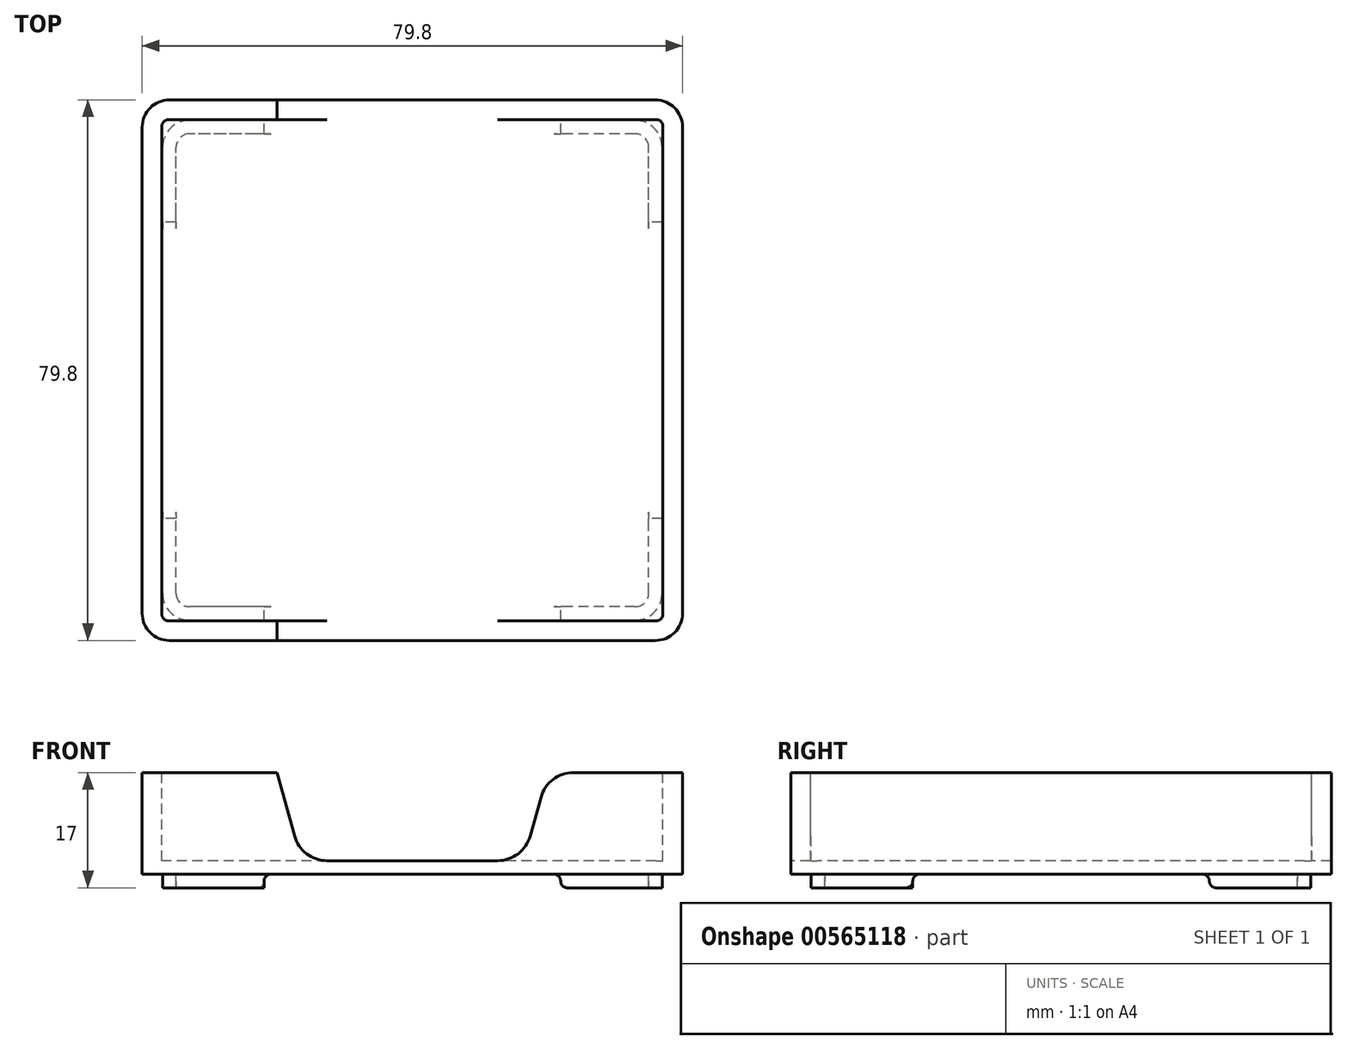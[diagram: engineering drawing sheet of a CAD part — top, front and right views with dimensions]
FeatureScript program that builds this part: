
annotation { "Feature Type Name" : "Feature", "Feature Type Description" : "" }
export const myFeature = defineFeature(function(context is Context, id is Id, definition is map)
    precondition{}
    {
        {
            var Q0;
            Q0=qCreatedBy(makeId("Top.planeOp"),FACE);
            var sketch = newSketch(context, id + "F0", { "sketchPlane" : qUnion([Q0])});
            skLineSegment(sketch, "E0.bottom", {"start": v(39.9, 39.9) * mm, "end": v(-39.9, 39.9) * mm});
            skLineSegment(sketch, "E0.top", {"start": v(39.9, -39.9) * mm, "end": v(-39.9, -39.9) * mm});
            skLineSegment(sketch, "E0.left", {"start": v(39.9, 39.9) * mm, "end": v(39.9, -39.9) * mm});
            skLineSegment(sketch, "E0.right", {"start": v(-39.9, 39.9) * mm, "end": v(-39.9, -39.9) * mm});
            skPoint(sketch, "E0.middle", {"position": v(0, 0) * mm});
            skSolve(sketch);
        }
        {
            var Q0;
            Q0=makeQuery(id+"F0.imprint","IMPRINT",FACE,{"disambiguationData":[TD([[makeQuery(id+"F0.imprint","IMPRINT",EDGE,{"derivedFrom":sQuery(id+"F0.wireOp",EDGE,"E0.bottom")}),1.0]])]});
            extrude(context, id + "F1", {"entities" : qUnion([Q0]), "depth" : 15 * mm, "offsetDistance" : 25 * mm});
        }
        {
            var Q0;
            Q0=makeQuery(id+"F1.opExtrude","CAP_FACE",FACE,{"disambiguationData":[OSD([sQuery(id+"F0.wireOp",EDGE,"E0.bottom"),sQuery(id+"F0.wireOp",EDGE,"E0.top"),sQuery(id+"F0.wireOp",EDGE,"E0.left"),sQuery(id+"F0.wireOp",EDGE,"E0.right")])],"isStart":false});
            var sketch = newSketch(context, id + "F2", { "sketchPlane" : qUnion([Q0])});
            skLineSegment(sketch, "E1.bottom", {"start": v(37, 37) * mm, "end": v(-37, 37) * mm});
            skLineSegment(sketch, "E1.top", {"start": v(37, -37) * mm, "end": v(-37, -37) * mm});
            skLineSegment(sketch, "E1.left", {"start": v(37, 37) * mm, "end": v(37, -37) * mm});
            skLineSegment(sketch, "E1.right", {"start": v(-37, 37) * mm, "end": v(-37, -37) * mm});
            skPoint(sketch, "E1.middle", {"position": v(0, 0) * mm});
            skSolve(sketch);
        }
        {
            var Q0;
            Q0=qSketchRegion(id+"F2",true);
            extrude(context, id + "F3", {"entities" : qUnion([Q0]), "operationType" : NewBodyOperationType.REMOVE, "oppositeDirection" : true, "depth" : 13 * mm, "offsetDistance" : 25 * mm});
        }
        {
            var Q0;
            Q0=makeQuery(id+"F1.opExtrude","CAP_FACE",FACE,{"disambiguationData":[OSD([sQuery(id+"F0.wireOp",EDGE,"E0.bottom"),sQuery(id+"F0.wireOp",EDGE,"E0.top"),sQuery(id+"F0.wireOp",EDGE,"E0.left"),sQuery(id+"F0.wireOp",EDGE,"E0.right")])],"isStart":true});
            var sketch = newSketch(context, id + "F4", { "sketchPlane" : qUnion([Q0])});
            skLineSegment(sketch, "E2.bottom", {"start": v(36.9, 36.9) * mm, "end": v(-36.9, 36.9) * mm});
            skLineSegment(sketch, "E2.top", {"start": v(36.9, -36.9) * mm, "end": v(-36.9, -36.9) * mm});
            skLineSegment(sketch, "E2.left", {"start": v(36.9, 36.9) * mm, "end": v(36.9, -36.9) * mm});
            skLineSegment(sketch, "E2.right", {"start": v(-36.9, 36.9) * mm, "end": v(-36.9, -36.9) * mm});
            skPoint(sketch, "E2.middle", {"position": v(0, 0) * mm});
            skLineSegment(sketch, "E3.bottom", {"start": v(34.9, 34.9) * mm, "end": v(-34.9, 34.9) * mm});
            skLineSegment(sketch, "E3.top", {"start": v(34.9, -34.9) * mm, "end": v(-34.9, -34.9) * mm});
            skLineSegment(sketch, "E3.left", {"start": v(34.9, 34.9) * mm, "end": v(34.9, -34.9) * mm});
            skLineSegment(sketch, "E3.right", {"start": v(-34.9, 34.9) * mm, "end": v(-34.9, -34.9) * mm});
            skSolve(sketch);
        }
        {
            var Q0;
            Q0=qSketchRegion(id+"F4",true);
            extrude(context, id + "F5", {"entities" : qUnion([Q0]), "operationType" : NewBodyOperationType.ADD, "depth" : 2 * mm, "offsetDistance" : 25 * mm});
        }
        {
            var Q0;
            Q0=makeQuery(id+"F5.opExtrude","CAP_FACE",FACE,{"disambiguationData":[OSD([sQuery(id+"F4.wireOp",EDGE,"E2.bottom"),sQuery(id+"F4.wireOp",EDGE,"E2.top"),sQuery(id+"F4.wireOp",EDGE,"E2.left"),sQuery(id+"F4.wireOp",EDGE,"E2.right"),sQuery(id+"F4.wireOp",EDGE,"E3.bottom"),sQuery(id+"F4.wireOp",EDGE,"E3.top"),sQuery(id+"F4.wireOp",EDGE,"E3.left"),sQuery(id+"F4.wireOp",EDGE,"E3.right")])],"isStart":false});
            var sketch = newSketch(context, id + "F6", { "sketchPlane" : qUnion([Q0])});
            skLineSegment(sketch, "E4.bottom", {"start": v(36.9, 21.9) * mm, "end": v(21.9, 21.9) * mm});
            skLineSegment(sketch, "E4.top", {"start": v(36.9, -21.9) * mm, "end": v(21.9, -21.9) * mm});
            skLineSegment(sketch, "E4.left", {"start": v(36.9, 21.9) * mm, "end": v(36.9, -21.9) * mm});
            skLineSegment(sketch, "E4.right", {"start": v(-36.9, 21.9) * mm, "end": v(-36.9, -21.9) * mm});
            skPoint(sketch, "E4.middle", {"position": v(0, 0) * mm});
            skLineSegment(sketch, "E5.bottom", {"start": v(-21.9, 36.9) * mm, "end": v(21.9, 36.9) * mm});
            skLineSegment(sketch, "E5.top", {"start": v(-21.9, -36.9) * mm, "end": v(21.9, -36.9) * mm});
            skLineSegment(sketch, "E5.left", {"start": v(-21.9, 36.9) * mm, "end": v(-21.9, 21.9) * mm});
            skLineSegment(sketch, "E5.right", {"start": v(21.9, 36.9) * mm, "end": v(21.9, 21.9) * mm});
            skLineSegment(sketch, "E6.trimOffspring", {"start": v(-21.9, -21.9) * mm, "end": v(-21.9, -36.9) * mm});
            skLineSegment(sketch, "E7.trimOffspring", {"start": v(-21.9, 21.9) * mm, "end": v(-36.9, 21.9) * mm});
            skLineSegment(sketch, "E8.trimOffspring", {"start": v(21.9, -21.9) * mm, "end": v(21.9, -36.9) * mm});
            skLineSegment(sketch, "E9.trimOffspring", {"start": v(-21.9, -21.9) * mm, "end": v(-36.9, -21.9) * mm});
            skSolve(sketch);
        }
        {
            var Q0;
            Q0=qSketchRegion(id+"F6",true);
            var Q1;
            Q1=makeQuery(id+"F5.boolean.opBoolean","SPLIT",FACE,{"disambiguationData":[TD([makeQuery(id+"F5.opExtrude","SWEPT_FACE",FACE,{"disambiguationData":[OSD([sQuery(id+"F4.wireOp",EDGE,"E3.bottom")])]})])],"derivedFrom":makeQuery(id+"F1.opExtrude","CAP_FACE",FACE,{"disambiguationData":[OSD([sQuery(id+"F0.wireOp",EDGE,"E0.bottom"),sQuery(id+"F0.wireOp",EDGE,"E0.top"),sQuery(id+"F0.wireOp",EDGE,"E0.left"),sQuery(id+"F0.wireOp",EDGE,"E0.right")])],"isStart":true})});
            extrude(context, id + "F7", {"entities" : qUnion([Q0]), "operationType" : NewBodyOperationType.REMOVE, "endBound" : BoundingType.UP_TO_SURFACE, "oppositeDirection" : true, "depth" : 25 * mm, "endBoundEntityFace" : qUnion([Q1]), "offsetDistance" : 25 * mm});
        }
        {
            var Q0;
            Q0=makeQuery(id+"F5.opExtrude","SWEPT_EDGE",EDGE,{"disambiguationData":[OSD([sQuery(id+"F4.wireOp",EDGE,"E3.top"),sQuery(id+"F4.wireOp",EDGE,"E3.right")])]});
            var Q1;
            Q1=makeQuery(id+"F5.opExtrude","SWEPT_EDGE",EDGE,{"disambiguationData":[OSD([sQuery(id+"F4.wireOp",EDGE,"E3.bottom"),sQuery(id+"F4.wireOp",EDGE,"E3.right")])]});
            var Q2;
            Q2=makeQuery(id+"F5.opExtrude","SWEPT_EDGE",EDGE,{"disambiguationData":[OSD([sQuery(id+"F4.wireOp",EDGE,"E3.bottom"),sQuery(id+"F4.wireOp",EDGE,"E3.left")])]});
            var Q3;
            Q3=makeQuery(id+"F5.opExtrude","SWEPT_EDGE",EDGE,{"disambiguationData":[OSD([sQuery(id+"F4.wireOp",EDGE,"E3.top"),sQuery(id+"F4.wireOp",EDGE,"E3.left")])]});
            fillet(context, id + "F8", {"entities" : qUnion([Q0, Q1, Q2, Q3]), "radius" : 2 * mm, "tangentPropagation" : true, "allowEdgeOverflow" : false});
        }
        {
            var Q0;
            Q0=makeQuery(id+"F5.opExtrude","SWEPT_EDGE",EDGE,{"disambiguationData":[OSD([sQuery(id+"F4.wireOp",EDGE,"E2.top"),sQuery(id+"F4.wireOp",EDGE,"E2.right")])]});
            var Q1;
            Q1=makeQuery(id+"F5.opExtrude","SWEPT_EDGE",EDGE,{"disambiguationData":[OSD([sQuery(id+"F4.wireOp",EDGE,"E2.top"),sQuery(id+"F4.wireOp",EDGE,"E2.left")])]});
            var Q2;
            Q2=makeQuery(id+"F5.opExtrude","SWEPT_EDGE",EDGE,{"disambiguationData":[OSD([sQuery(id+"F4.wireOp",EDGE,"E2.bottom"),sQuery(id+"F4.wireOp",EDGE,"E2.left")])]});
            var Q3;
            Q3=makeQuery(id+"F5.opExtrude","SWEPT_EDGE",EDGE,{"disambiguationData":[OSD([sQuery(id+"F4.wireOp",EDGE,"E2.bottom"),sQuery(id+"F4.wireOp",EDGE,"E2.right")])]});
            fillet(context, id + "F9", {"entities" : qUnion([Q0, Q1, Q2, Q3]), "radius" : 4 * mm, "tangentPropagation" : true, "allowEdgeOverflow" : false});
        }
        {
            var Q0;
            Q0=makeQuery(id+"F7.boolean.opBoolean","COPY",EDGE,{"derivedFrom":makeQuery(id+"F7.opExtrude","CAP_EDGE",EDGE,{"disambiguationData":[OSD([sQuery(id+"F6.wireOp",EDGE,"E5.right")])],"isStart":true})});
            var Q1;
            Q1=makeQuery(id+"F7.boolean.opBoolean","COPY",EDGE,{"derivedFrom":makeQuery(id+"F7.opExtrude","CAP_EDGE",EDGE,{"disambiguationData":[OSD([sQuery(id+"F6.wireOp",EDGE,"E5.right")])],"isStart":false})});
            var Q2;
            Q2=makeQuery(id+"F7.boolean.opBoolean","COPY",EDGE,{"derivedFrom":makeQuery(id+"F7.opExtrude","CAP_EDGE",EDGE,{"disambiguationData":[OSD([sQuery(id+"F6.wireOp",EDGE,"E4.bottom")])],"isStart":true})});
            var Q3;
            Q3=makeQuery(id+"F7.boolean.opBoolean","COPY",EDGE,{"derivedFrom":makeQuery(id+"F7.opExtrude","CAP_EDGE",EDGE,{"disambiguationData":[OSD([sQuery(id+"F6.wireOp",EDGE,"E4.bottom")])],"isStart":false})});
            var Q4;
            Q4=makeQuery(id+"F7.boolean.opBoolean","COPY",EDGE,{"derivedFrom":makeQuery(id+"F7.opExtrude","CAP_EDGE",EDGE,{"disambiguationData":[OSD([sQuery(id+"F6.wireOp",EDGE,"E7.trimOffspring")])],"isStart":true})});
            var Q5;
            Q5=makeQuery(id+"F7.boolean.opBoolean","COPY",EDGE,{"derivedFrom":makeQuery(id+"F7.opExtrude","CAP_EDGE",EDGE,{"disambiguationData":[OSD([sQuery(id+"F6.wireOp",EDGE,"E7.trimOffspring")])],"isStart":false})});
            var Q6;
            Q6=makeQuery(id+"F7.boolean.opBoolean","COPY",EDGE,{"derivedFrom":makeQuery(id+"F7.opExtrude","CAP_EDGE",EDGE,{"disambiguationData":[OSD([sQuery(id+"F6.wireOp",EDGE,"E5.left")])],"isStart":true})});
            var Q7;
            Q7=makeQuery(id+"F7.boolean.opBoolean","COPY",EDGE,{"derivedFrom":makeQuery(id+"F7.opExtrude","CAP_EDGE",EDGE,{"disambiguationData":[OSD([sQuery(id+"F6.wireOp",EDGE,"E5.left")])],"isStart":false})});
            var Q8;
            Q8=makeQuery(id+"F7.boolean.opBoolean","COPY",EDGE,{"derivedFrom":makeQuery(id+"F7.opExtrude","CAP_EDGE",EDGE,{"disambiguationData":[OSD([sQuery(id+"F6.wireOp",EDGE,"E9.trimOffspring")])],"isStart":true})});
            var Q9;
            Q9=makeQuery(id+"F7.boolean.opBoolean","COPY",EDGE,{"derivedFrom":makeQuery(id+"F7.opExtrude","CAP_EDGE",EDGE,{"disambiguationData":[OSD([sQuery(id+"F6.wireOp",EDGE,"E9.trimOffspring")])],"isStart":false})});
            var Q10;
            Q10=makeQuery(id+"F7.boolean.opBoolean","COPY",EDGE,{"derivedFrom":makeQuery(id+"F7.opExtrude","CAP_EDGE",EDGE,{"disambiguationData":[OSD([sQuery(id+"F6.wireOp",EDGE,"E6.trimOffspring")])],"isStart":true})});
            var Q11;
            Q11=makeQuery(id+"F7.boolean.opBoolean","COPY",EDGE,{"derivedFrom":makeQuery(id+"F7.opExtrude","CAP_EDGE",EDGE,{"disambiguationData":[OSD([sQuery(id+"F6.wireOp",EDGE,"E6.trimOffspring")])],"isStart":false})});
            var Q12;
            Q12=makeQuery(id+"F7.boolean.opBoolean","COPY",EDGE,{"derivedFrom":makeQuery(id+"F7.opExtrude","CAP_EDGE",EDGE,{"disambiguationData":[OSD([sQuery(id+"F6.wireOp",EDGE,"E8.trimOffspring")])],"isStart":true})});
            var Q13;
            Q13=makeQuery(id+"F7.boolean.opBoolean","COPY",EDGE,{"derivedFrom":makeQuery(id+"F7.opExtrude","CAP_EDGE",EDGE,{"disambiguationData":[OSD([sQuery(id+"F6.wireOp",EDGE,"E8.trimOffspring")])],"isStart":false})});
            var Q14;
            Q14=makeQuery(id+"F7.boolean.opBoolean","COPY",EDGE,{"derivedFrom":makeQuery(id+"F7.opExtrude","CAP_EDGE",EDGE,{"disambiguationData":[OSD([sQuery(id+"F6.wireOp",EDGE,"E4.top")])],"isStart":true})});
            var Q15;
            Q15=makeQuery(id+"F7.boolean.opBoolean","COPY",EDGE,{"derivedFrom":makeQuery(id+"F7.opExtrude","CAP_EDGE",EDGE,{"disambiguationData":[OSD([sQuery(id+"F6.wireOp",EDGE,"E4.top")])],"isStart":false})});
            var Q16;
            Q16=makeQuery(id+"F7.boolean.opBoolean","COPY",EDGE,{"derivedFrom":makeQuery(id+"F7.opExtrude","CAP_EDGE",EDGE,{"disambiguationData":[OSD([sQuery(id+"F6.wireOp",EDGE,"E4.top")])],"isStart":false})});
            fillet(context, id + "F10", {"entities" : qUnion([Q0, Q1, Q2, Q3, Q4, Q5, Q6, Q7, Q8, Q9, Q10, Q11, Q12, Q13, Q14, Q15, Q16]), "radius" : 1 * mm, "tangentPropagation" : true, "allowEdgeOverflow" : false});
        }
        {
            var Q0;
            Q0=makeQuery(id+"F1.opExtrude","SWEPT_FACE",FACE,{"disambiguationData":[OSD([sQuery(id+"F0.wireOp",EDGE,"E0.top")])]});
            var sketch = newSketch(context, id + "F11", { "sketchPlane" : qUnion([Q0])});
            skLineSegment(sketch, "E10", {"start": v(-22.33, 15) * mm, "end": v(44.47, 15) * mm, "construction": true});
            skLineSegment(sketch, "E11", {"start": v(-15.04, -30) * mm, "end": v(49.84, -30) * mm, "construction": true});
            skLineSegment(sketch, "E12", {"start": v(-20, 15) * mm, "end": v(-16.39, 2) * mm});
            skLineSegment(sketch, "E13", {"start": v(20, 15) * mm, "end": v(16.39, 2) * mm});
            skLineSegment(sketch, "E14", {"start": v(-16.39, 2) * mm, "end": v(16.39, 2) * mm});
            skLineSegment(sketch, "E15", {"start": v(-20, 15) * mm, "end": v(20, 15) * mm});
            skLineSegment(sketch, "E16", {"start": v(-16.39, 2) * mm, "end": v(-7.5, -30) * mm, "construction": true});
            skLineSegment(sketch, "E17", {"start": v(16.39, 2) * mm, "end": v(7.5, -30) * mm, "construction": true});
            skSolve(sketch);
        }
        {
            var Q0;
            Q0=qSketchRegion(id+"F11",true);
            extrude(context, id + "F12", {"entities" : qUnion([Q0]), "operationType" : NewBodyOperationType.REMOVE, "endBound" : BoundingType.THROUGH_ALL, "oppositeDirection" : true, "depth" : 25 * mm, "offsetDistance" : 25 * mm});
        }
        {
            var Q0;
            {var subQ0=sQuery(id+"F0.wireOp",EDGE,"E0.top");var subQ1=sQuery(id+"F11.wireOp",EDGE,"E12");Q0=makeQuery(id+"F12.boolean.opBoolean","COPY",EDGE,{"disambiguationData":[TD([makeQuery(id+"F1.opExtrude","SWEPT_FACE",FACE,{"disambiguationData":[OSD([subQ0])]})])],"derivedFrom":makeQuery(id+"F12.opExtrude","SWEPT_EDGE",EDGE,{"disambiguationData":[OSD([subQ0,subQ1,sQuery(id+"F11.wireOp",EDGE,"E15")])]})});}
            var Q1;
            {var subQ1=sQuery(id+"F11.wireOp",EDGE,"E12");var subQ2=sQuery(id+"F11.wireOp",EDGE,"E14");Q1=makeQuery(id+"F12.boolean.opBoolean","COPY",EDGE,{"disambiguationData":[TD([makeQuery(id+"F1.opExtrude","SWEPT_FACE",FACE,{"disambiguationData":[OSD([sQuery(id+"F0.wireOp",EDGE,"E0.top")])]})])],"derivedFrom":makeQuery(id+"F12.opExtrude","SWEPT_EDGE",EDGE,{"disambiguationData":[OSD([subQ1,subQ2])]})});}
            var Q2;
            {var subQ0=sQuery(id+"F11.wireOp",EDGE,"E13");var subQ2=sQuery(id+"F11.wireOp",EDGE,"E14");Q2=makeQuery(id+"F12.boolean.opBoolean","COPY",EDGE,{"disambiguationData":[TD([makeQuery(id+"F1.opExtrude","SWEPT_FACE",FACE,{"disambiguationData":[OSD([sQuery(id+"F0.wireOp",EDGE,"E0.top")])]})])],"derivedFrom":makeQuery(id+"F12.opExtrude","SWEPT_EDGE",EDGE,{"disambiguationData":[OSD([subQ0,subQ2])]})});}
            var Q3;
            {var subQ0=sQuery(id+"F0.wireOp",EDGE,"E0.top");var subQ1=sQuery(id+"F11.wireOp",EDGE,"E13");Q3=makeQuery(id+"F12.boolean.opBoolean","COPY",EDGE,{"disambiguationData":[TD([makeQuery(id+"F1.opExtrude","SWEPT_FACE",FACE,{"disambiguationData":[OSD([subQ0])]})])],"derivedFrom":makeQuery(id+"F12.opExtrude","SWEPT_EDGE",EDGE,{"disambiguationData":[OSD([subQ0,subQ1,sQuery(id+"F11.wireOp",EDGE,"E15")])]})});}
            var Q4;
            {var subQ0=sQuery(id+"F11.wireOp",EDGE,"E13");var subQ2=sQuery(id+"F11.wireOp",EDGE,"E14");Q4=makeQuery(id+"F12.boolean.opBoolean","COPY",EDGE,{"disambiguationData":[TD([makeQuery(id+"F1.opExtrude","SWEPT_FACE",FACE,{"disambiguationData":[OSD([sQuery(id+"F0.wireOp",EDGE,"E0.bottom")])]})])],"derivedFrom":makeQuery(id+"F12.opExtrude","SWEPT_EDGE",EDGE,{"disambiguationData":[OSD([subQ0,subQ2])]})});}
            var Q5;
            {var subQ0=sQuery(id+"F0.wireOp",EDGE,"E0.bottom");var subQ1=sQuery(id+"F0.wireOp",EDGE,"E0.top");var subQ2=sQuery(id+"F11.wireOp",EDGE,"E13");Q5=makeQuery(id+"F12.boolean.opBoolean","COPY",EDGE,{"disambiguationData":[TD([makeQuery(id+"F1.opExtrude","SWEPT_FACE",FACE,{"disambiguationData":[OSD([subQ0])]})])],"derivedFrom":makeQuery(id+"F12.opExtrude","SWEPT_EDGE",EDGE,{"disambiguationData":[OSD([subQ1,subQ2,sQuery(id+"F11.wireOp",EDGE,"E15")])]})});}
            var Q6;
            {var subQ0=sQuery(id+"F0.wireOp",EDGE,"E0.bottom");var subQ1=sQuery(id+"F0.wireOp",EDGE,"E0.top");var subQ2=sQuery(id+"F11.wireOp",EDGE,"E12");Q6=makeQuery(id+"F12.boolean.opBoolean","COPY",EDGE,{"disambiguationData":[TD([makeQuery(id+"F1.opExtrude","SWEPT_FACE",FACE,{"disambiguationData":[OSD([subQ0])]})])],"derivedFrom":makeQuery(id+"F12.opExtrude","SWEPT_EDGE",EDGE,{"disambiguationData":[OSD([subQ1,subQ2,sQuery(id+"F11.wireOp",EDGE,"E15")])]})});}
            var Q7;
            {var subQ0=sQuery(id+"F11.wireOp",EDGE,"E12");var subQ2=sQuery(id+"F11.wireOp",EDGE,"E14");Q7=makeQuery(id+"F12.boolean.opBoolean","COPY",EDGE,{"disambiguationData":[TD([makeQuery(id+"F1.opExtrude","SWEPT_FACE",FACE,{"disambiguationData":[OSD([sQuery(id+"F0.wireOp",EDGE,"E0.bottom")])]})])],"derivedFrom":makeQuery(id+"F12.opExtrude","SWEPT_EDGE",EDGE,{"disambiguationData":[OSD([subQ0,subQ2])]})});}
            fillet(context, id + "F13", {"entities" : qUnion([Q0, Q1, Q2, Q3, Q4, Q5, Q6, Q7]), "radius" : 5 * mm, "tangentPropagation" : true, "allowEdgeOverflow" : false});
        }
        {
            var Q0;
            Q0=makeQuery(id+"F1.opExtrude","SWEPT_EDGE",EDGE,{"disambiguationData":[OSD([sQuery(id+"F0.wireOp",EDGE,"E0.top"),sQuery(id+"F0.wireOp",EDGE,"E0.left")])]});
            var Q1;
            Q1=makeQuery(id+"F1.opExtrude","SWEPT_EDGE",EDGE,{"disambiguationData":[OSD([sQuery(id+"F0.wireOp",EDGE,"E0.bottom"),sQuery(id+"F0.wireOp",EDGE,"E0.left")])]});
            var Q2;
            Q2=makeQuery(id+"F1.opExtrude","SWEPT_EDGE",EDGE,{"disambiguationData":[OSD([sQuery(id+"F0.wireOp",EDGE,"E0.top"),sQuery(id+"F0.wireOp",EDGE,"E0.right")])]});
            var Q3;
            Q3=makeQuery(id+"F1.opExtrude","SWEPT_EDGE",EDGE,{"disambiguationData":[OSD([sQuery(id+"F0.wireOp",EDGE,"E0.bottom"),sQuery(id+"F0.wireOp",EDGE,"E0.right")])]});
            fillet(context, id + "F14", {"entities" : qUnion([Q0, Q1, Q2, Q3]), "radius" : 4 * mm, "tangentPropagation" : true, "allowEdgeOverflow" : false});
        }
        {
            var Q0;
            Q0=makeQuery(id+"F3.boolean.opBoolean","COPY",EDGE,{"derivedFrom":makeQuery(id+"F3.opExtrude","SWEPT_EDGE",EDGE,{"disambiguationData":[OSD([sQuery(id+"F2.wireOp",EDGE,"E1.bottom"),sQuery(id+"F2.wireOp",EDGE,"E1.left")])]})});
            var Q1;
            Q1=makeQuery(id+"F3.boolean.opBoolean","COPY",EDGE,{"derivedFrom":makeQuery(id+"F3.opExtrude","SWEPT_EDGE",EDGE,{"disambiguationData":[OSD([sQuery(id+"F2.wireOp",EDGE,"E1.bottom"),sQuery(id+"F2.wireOp",EDGE,"E1.right")])]})});
            var Q2;
            Q2=makeQuery(id+"F3.boolean.opBoolean","COPY",EDGE,{"derivedFrom":makeQuery(id+"F3.opExtrude","SWEPT_EDGE",EDGE,{"disambiguationData":[OSD([sQuery(id+"F2.wireOp",EDGE,"E1.top"),sQuery(id+"F2.wireOp",EDGE,"E1.right")])]})});
            var Q3;
            Q3=makeQuery(id+"F3.boolean.opBoolean","COPY",EDGE,{"derivedFrom":makeQuery(id+"F3.opExtrude","SWEPT_EDGE",EDGE,{"disambiguationData":[OSD([sQuery(id+"F2.wireOp",EDGE,"E1.top"),sQuery(id+"F2.wireOp",EDGE,"E1.left")])]})});
            fillet(context, id + "F15", {"entities" : qUnion([Q0, Q1, Q2, Q3]), "radius" : 1 * mm, "tangentPropagation" : true, "allowEdgeOverflow" : false});
        }
    });
